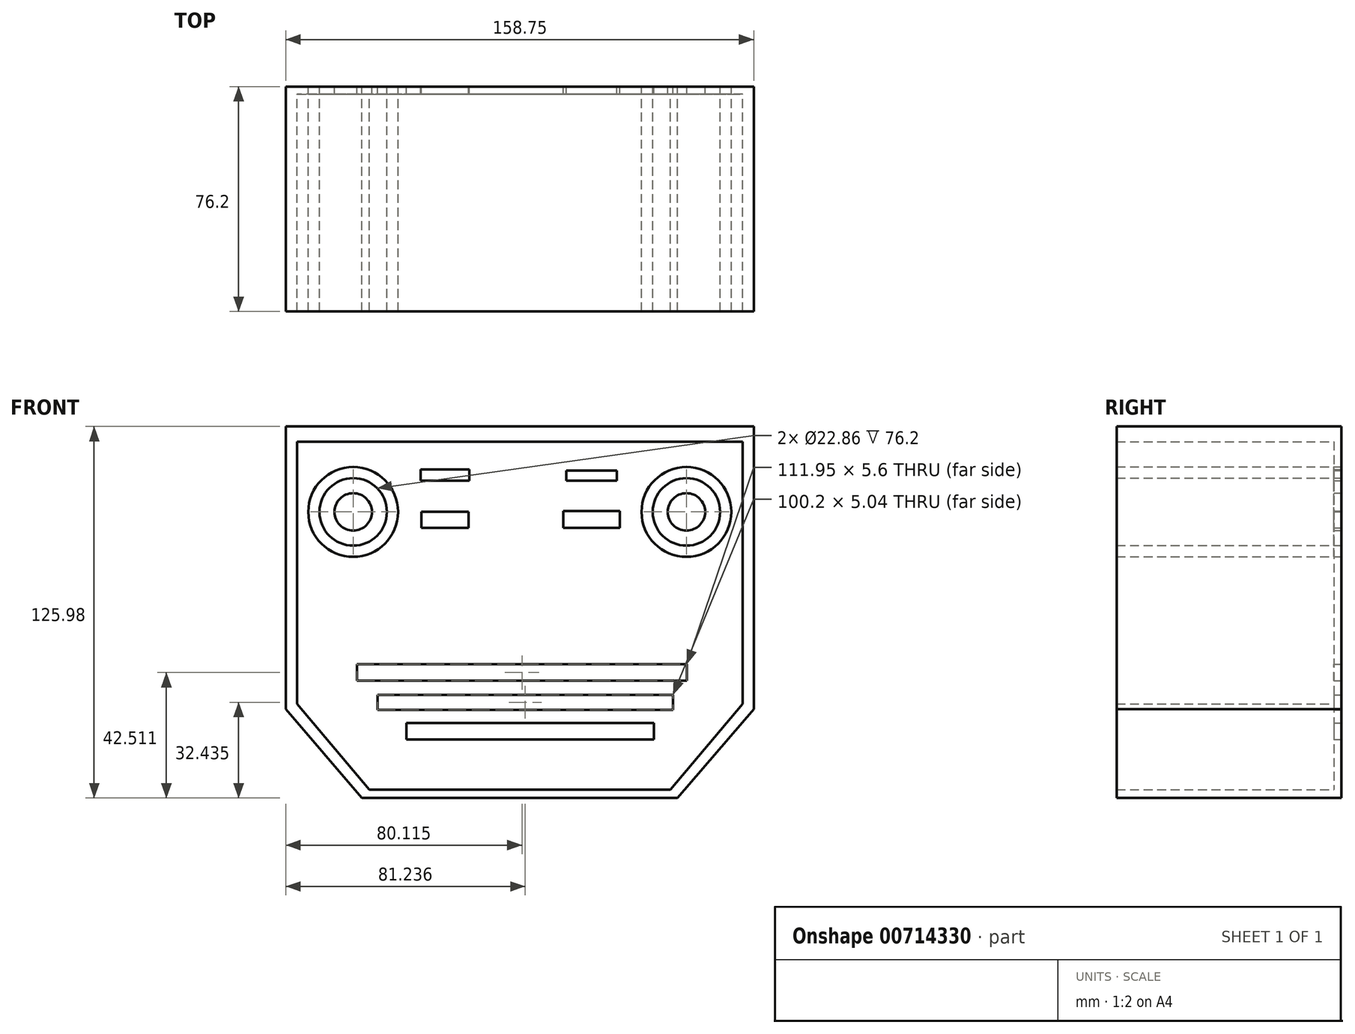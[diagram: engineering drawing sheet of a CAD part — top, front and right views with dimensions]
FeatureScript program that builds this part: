
annotation { "Feature Type Name" : "Feature", "Feature Type Description" : "" }
export const myFeature = defineFeature(function(context is Context, id is Id, definition is map)
    precondition{}
    {
        {
            var Q0;
            Q0=qCreatedBy(makeId("Front.planeOp"),FACE);
            var sketch = newSketch(context, id + "F0", { "sketchPlane" : qUnion([Q0])});
            skCircle(sketch, "E0", {"center": v(-36.2, 48.37) * mm, "radius": 11.43 * mm});
            skCircle(sketch, "E1", {"center": v(76.82, 48.37) * mm, "radius": 11.43 * mm});
            skLineSegment(sketch, "E2", {"start": v(-55.26, 72.19) * mm, "end": v(95.87, 72.19) * mm});
            skLineSegment(sketch, "E3", {"start": v(95.87, 72.19) * mm, "end": v(95.87, -16.71) * mm});
            skLineSegment(sketch, "E4", {"start": v(95.87, -16.71) * mm, "end": v(71.32, -45.85) * mm});
            skLineSegment(sketch, "E5", {"start": v(71.32, -45.85) * mm, "end": v(-30.7, -45.85) * mm});
            skLineSegment(sketch, "E6", {"start": v(-30.7, -45.85) * mm, "end": v(-55.26, -16.71) * mm});
            skLineSegment(sketch, "E7", {"start": v(-55.26, 72.19) * mm, "end": v(-55.26, -16.71) * mm});
            skCircle(sketch, "E8", {"center": v(76.82, 48.37) * mm, "radius": 15.24 * mm});
            skCircle(sketch, "E9", {"center": v(-36.2, 48.37) * mm, "radius": 15.24 * mm});
            skLineSegment(sketch, "E10", {"start": v(-59.08, 77.35) * mm, "end": v(-59.08, -18.53) * mm});
            skLineSegment(sketch, "E11", {"start": v(-59.08, -18.53) * mm, "end": v(-33.24, -48.63) * mm});
            skLineSegment(sketch, "E12", {"start": v(-33.24, -48.63) * mm, "end": v(73.82, -48.63) * mm});
            skLineSegment(sketch, "E13", {"start": v(73.82, -48.63) * mm, "end": v(99.67, -18.53) * mm});
            skLineSegment(sketch, "E14", {"start": v(99.67, -18.53) * mm, "end": v(99.67, 77.35) * mm});
            skLineSegment(sketch, "E15", {"start": v(99.67, 77.35) * mm, "end": v(-59.08, 77.35) * mm});
            skCircle(sketch, "E16", {"center": v(-36.2, 48.37) * mm, "radius": 6.35 * mm});
            skCircle(sketch, "E17", {"center": v(76.82, 48.37) * mm, "radius": 6.35 * mm});
            skLineSegment(sketch, "E18", {"start": v(-34.94, -3.32) * mm, "end": v(77.01, -3.32) * mm});
            skLineSegment(sketch, "E19", {"start": v(77.01, -3.32) * mm, "end": v(77.01, -8.92) * mm});
            skLineSegment(sketch, "E20", {"start": v(77.01, -8.92) * mm, "end": v(-34.94, -8.92) * mm});
            skLineSegment(sketch, "E21", {"start": v(-34.94, -8.92) * mm, "end": v(-34.94, -3.32) * mm});
            skLineSegment(sketch, "E22", {"start": v(-27.94, -13.68) * mm, "end": v(-27.94, -18.71) * mm});
            skLineSegment(sketch, "E23", {"start": v(-27.94, -18.71) * mm, "end": v(72.26, -18.71) * mm});
            skLineSegment(sketch, "E24", {"start": v(72.26, -18.71) * mm, "end": v(72.26, -13.68) * mm});
            skLineSegment(sketch, "E25", {"start": v(72.26, -13.68) * mm, "end": v(-27.94, -13.68) * mm});
            skLineSegment(sketch, "E26", {"start": v(-18.2, -23.2) * mm, "end": v(-18.2, -28.8) * mm});
            skLineSegment(sketch, "E27", {"start": v(-18.2, -28.8) * mm, "end": v(65.73, -28.8) * mm});
            skLineSegment(sketch, "E28", {"start": v(65.73, -28.8) * mm, "end": v(65.73, -23.2) * mm});
            skLineSegment(sketch, "E29", {"start": v(65.73, -23.2) * mm, "end": v(-18.2, -23.2) * mm});
            skLineSegment(sketch, "E30.bottom", {"start": v(-13.35, 62.74) * mm, "end": v(3.22, 62.74) * mm});
            skLineSegment(sketch, "E30.top", {"start": v(-13.35, 58.92) * mm, "end": v(3.22, 58.92) * mm});
            skLineSegment(sketch, "E30.left", {"start": v(-13.35, 62.74) * mm, "end": v(-13.35, 58.92) * mm});
            skLineSegment(sketch, "E30.right", {"start": v(3.22, 62.74) * mm, "end": v(3.22, 58.92) * mm});
            skLineSegment(sketch, "E31.bottom", {"start": v(-13.03, 42.98) * mm, "end": v(2.9, 42.98) * mm});
            skLineSegment(sketch, "E31.top", {"start": v(-13.03, 48.4) * mm, "end": v(2.9, 48.4) * mm});
            skLineSegment(sketch, "E31.left", {"start": v(-13.03, 42.98) * mm, "end": v(-13.03, 48.4) * mm});
            skLineSegment(sketch, "E31.right", {"start": v(2.9, 42.98) * mm, "end": v(2.9, 48.4) * mm});
            skLineSegment(sketch, "E32.bottom", {"start": v(2.9, 48.4) * mm, "end": v(2.9, 48.4) * mm});
            skLineSegment(sketch, "E32.top", {"start": v(2.9, 42.98) * mm, "end": v(2.9, 42.98) * mm});
            skLineSegment(sketch, "E32.left", {"start": v(2.9, 48.4) * mm, "end": v(2.9, 42.98) * mm});
            skLineSegment(sketch, "E32.right", {"start": v(2.9, 48.4) * mm, "end": v(2.9, 42.98) * mm});
            skLineSegment(sketch, "E33.bottom", {"start": v(36.04, 58.92) * mm, "end": v(53.25, 58.92) * mm});
            skLineSegment(sketch, "E33.top", {"start": v(36.04, 62.42) * mm, "end": v(53.25, 62.42) * mm});
            skLineSegment(sketch, "E33.left", {"start": v(36.04, 58.92) * mm, "end": v(36.04, 62.42) * mm});
            skLineSegment(sketch, "E33.right", {"start": v(53.25, 58.92) * mm, "end": v(53.25, 62.42) * mm});
            skLineSegment(sketch, "E34.bottom", {"start": v(35.09, 48.72) * mm, "end": v(54.21, 48.72) * mm});
            skLineSegment(sketch, "E34.top", {"start": v(35.09, 42.98) * mm, "end": v(54.21, 42.98) * mm});
            skLineSegment(sketch, "E34.left", {"start": v(35.09, 48.72) * mm, "end": v(35.09, 42.98) * mm});
            skLineSegment(sketch, "E34.right", {"start": v(54.21, 48.72) * mm, "end": v(54.21, 42.98) * mm});
            skSolve(sketch);
        }
        {
            var Q0;
            Q0 = qSketchRegion(id + "F0", true);
            var Q1;
            Q1=makeQuery(id+"F0.imprint","IMPRINT",FACE,{"disambiguationData":[TD([[makeQuery(id+"F0.imprint","IMPRINT",EDGE,{"derivedFrom":sQuery(id+"F0.wireOp",EDGE,"E16")}),1.0]])]});
            extrude(context, id + "F1", {"entities" : qUnion([Q0, Q1]), "depth" : 76.2 * mm, "offsetDistance" : 25.4 * mm});
        }
        {
            var Q0;
            Q0=makeQuery(id+"F1.opExtrude","SWEPT_BODY",BODY,{"disambiguationData":[OSD([sQuery(id+"F0.wireOp",EDGE,"E16")])]});
            deleteBodies(context, id + "F2", {"entities" : qUnion([Q0])});
        }
        {
            var Q0;
            Q0=makeQuery(id+"F0.imprint","IMPRINT",FACE,{"disambiguationData":[TD([[makeQuery(id+"F0.imprint","IMPRINT",EDGE,{"derivedFrom":sQuery(id+"F0.wireOp",EDGE,"E2")}),-1.0]])]});
            var Q1;
            Q1=makeQuery(id+"F0.imprint","IMPRINT",FACE,{"disambiguationData":[TD([[makeQuery(id+"F0.imprint","IMPRINT",EDGE,{"derivedFrom":sQuery(id+"F0.wireOp",EDGE,"E0")}),1.0]])]});
            var Q2;
            Q2=makeQuery(id+"F0.imprint","IMPRINT",FACE,{"disambiguationData":[TD([[makeQuery(id+"F0.imprint","IMPRINT",EDGE,{"derivedFrom":sQuery(id+"F0.wireOp",EDGE,"E1")}),1.0]])]});
            extrude(context, id + "F3", {"entities" : qUnion([Q0, Q1, Q2]), "operationType" : NewBodyOperationType.ADD, "depth" : 2.54 * mm, "offsetDistance" : 25.4 * mm});
        }
        {
            var Q0;
            Q0 = qSketchRegion(id + "F0", true);
            extrude(context, id + "F4", {"entities" : qUnion([Q0]), "operationType" : NewBodyOperationType.ADD, "depth" : 25.4 * mm, "offsetDistance" : 25.4 * mm});
        }
        {
            var Q0;
            Q0=makeQuery(id+"F0.imprint","IMPRINT",FACE,{"disambiguationData":[TD([[makeQuery(id+"F0.imprint","IMPRINT",EDGE,{"derivedFrom":sQuery(id+"F0.wireOp",EDGE,"E0")}),-1.0]])]});
            var Q1;
            Q1=makeQuery(id+"F0.imprint","IMPRINT",FACE,{"disambiguationData":[TD([[makeQuery(id+"F0.imprint","IMPRINT",EDGE,{"derivedFrom":sQuery(id+"F0.wireOp",EDGE,"E1")}),-1.0]])]});
            extrude(context, id + "F5", {"entities" : qUnion([Q0, Q1]), "depth" : 76.2 * mm, "offsetDistance" : 25.4 * mm});
        }
    });
